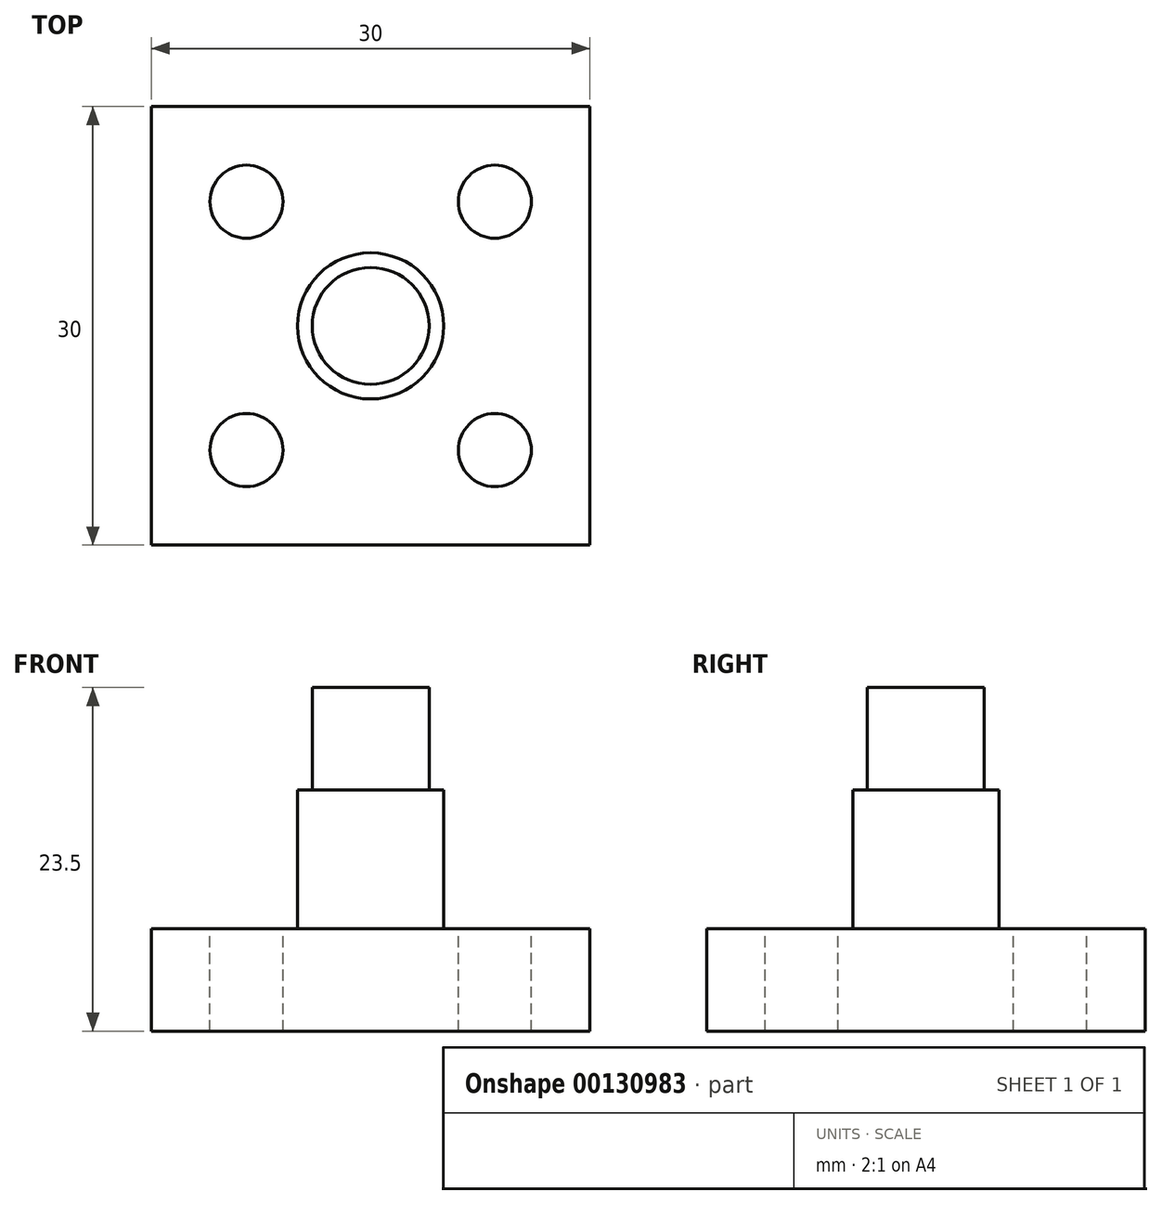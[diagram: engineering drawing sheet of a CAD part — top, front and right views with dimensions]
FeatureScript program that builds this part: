
annotation { "Feature Type Name" : "Feature", "Feature Type Description" : "" }
export const myFeature = defineFeature(function(context is Context, id is Id, definition is map)
    precondition{}
    {
        {
            var Q0;
            Q0=qCreatedBy(makeId("Top.planeOp"),FACE);
            var sketch = newSketch(context, id + "F0", { "sketchPlane" : qUnion([Q0])});
            skLineSegment(sketch, "E0.bottom", {"start": v(15, 15) * mm, "end": v(-15, 15) * mm});
            skLineSegment(sketch, "E0.top", {"start": v(15, -15) * mm, "end": v(-15, -15) * mm});
            skLineSegment(sketch, "E0.left", {"start": v(15, 15) * mm, "end": v(15, -15) * mm});
            skLineSegment(sketch, "E0.right", {"start": v(-15, 15) * mm, "end": v(-15, -15) * mm});
            skPoint(sketch, "E0.middle", {"position": v(0, 0) * mm});
            skCircle(sketch, "E1", {"center": v(0, 0) * mm, "radius": 4 * mm});
            skCircle(sketch, "E2.0", {"center": v(0, 0) * mm, "radius": 5 * mm});
            skSolve(sketch);
        }
        {
            var Q0;
            Q0=makeQuery(id+"F0.imprint","IMPRINT",FACE,{"disambiguationData":[TD([[makeQuery(id+"F0.imprint","IMPRINT",EDGE,{"derivedFrom":sQuery(id+"F0.wireOp",EDGE,"E0.bottom")}),1.0]])]});
            extrude(context, id + "F1", {"entities" : qUnion([Q0]), "depth" : 7 * mm});
        }
        {
            var Q0;
            Q0=makeQuery(id+"F0.imprint","IMPRINT",FACE,{"disambiguationData":[TD([[makeQuery(id+"F0.imprint","IMPRINT",EDGE,{"derivedFrom":sQuery(id+"F0.wireOp",EDGE,"E1")}),-1.0]])]});
            extrude(context, id + "F2", {"entities" : qUnion([Q0]), "operationType" : NewBodyOperationType.ADD, "depth" : 16.5 * mm});
        }
        {
            var Q0;
            Q0=makeQuery(id+"F0.imprint","IMPRINT",FACE,{"disambiguationData":[TD([[makeQuery(id+"F0.imprint","IMPRINT",EDGE,{"derivedFrom":sQuery(id+"F0.wireOp",EDGE,"E1")}),1.0]])]});
            extrude(context, id + "F3", {"entities" : qUnion([Q0]), "operationType" : NewBodyOperationType.ADD, "depth" : 23.5 * mm});
        }
        {
            var Q0;
            Q0=makeQuery(id+"F1.opExtrude","CAP_FACE",FACE,{"disambiguationData":[OSD([sQuery(id+"F0.wireOp",EDGE,"E0.bottom"),sQuery(id+"F0.wireOp",EDGE,"E0.top"),sQuery(id+"F0.wireOp",EDGE,"E0.left"),sQuery(id+"F0.wireOp",EDGE,"E0.right"),sQuery(id+"F0.wireOp",EDGE,"E2.0")])],"isStart":false});
            var sketch = newSketch(context, id + "F4", { "sketchPlane" : qUnion([Q0])});
            skPoint(sketch, "E3", {"position": v(8.5, 8.5) * mm});
            skPoint(sketch, "E4.1.0", {"position": v(-8.5, 8.5) * mm});
            skPoint(sketch, "E4.2.0", {"position": v(-8.5, -8.5) * mm});
            skPoint(sketch, "E4.3.0", {"position": v(8.5, -8.5) * mm});
            skPoint(sketch, "E4.center", {"position": v(0, 0) * mm});
            skSolve(sketch);
        }
        {
            var Q0;
            Q0=sQuery(id+"F4.wireOp",VERTEX,"E3");
            var Q1;
            Q1=sQuery(id+"F4.wireOp",VERTEX,"E4.1.0");
            var Q2;
            Q2=sQuery(id+"F4.wireOp",VERTEX,"E4.2.0");
            var Q3;
            Q3=sQuery(id+"F4.wireOp",VERTEX,"E4.3.0");
            var Q4;
            Q4=makeQuery(id+"F1.opExtrude","SWEPT_BODY",BODY,{"disambiguationData":[OSD([sQuery(id+"F0.wireOp",EDGE,"E0.bottom"),sQuery(id+"F0.wireOp",EDGE,"E0.top"),sQuery(id+"F0.wireOp",EDGE,"E0.left"),sQuery(id+"F0.wireOp",EDGE,"E0.right"),sQuery(id+"F0.wireOp",EDGE,"E2.0")])]});
            hole(context, id + "F5", {"style" : HoleStyle.SIMPLE, "endStyle" : HoleEndStyle.THROUGH, "holeDiameter" : 5 * mm, "locations" : qUnion([Q0, Q1, Q2, Q3]), "scope" : qUnion([Q4]), "isTappedThrough" : true});
        }
    });
